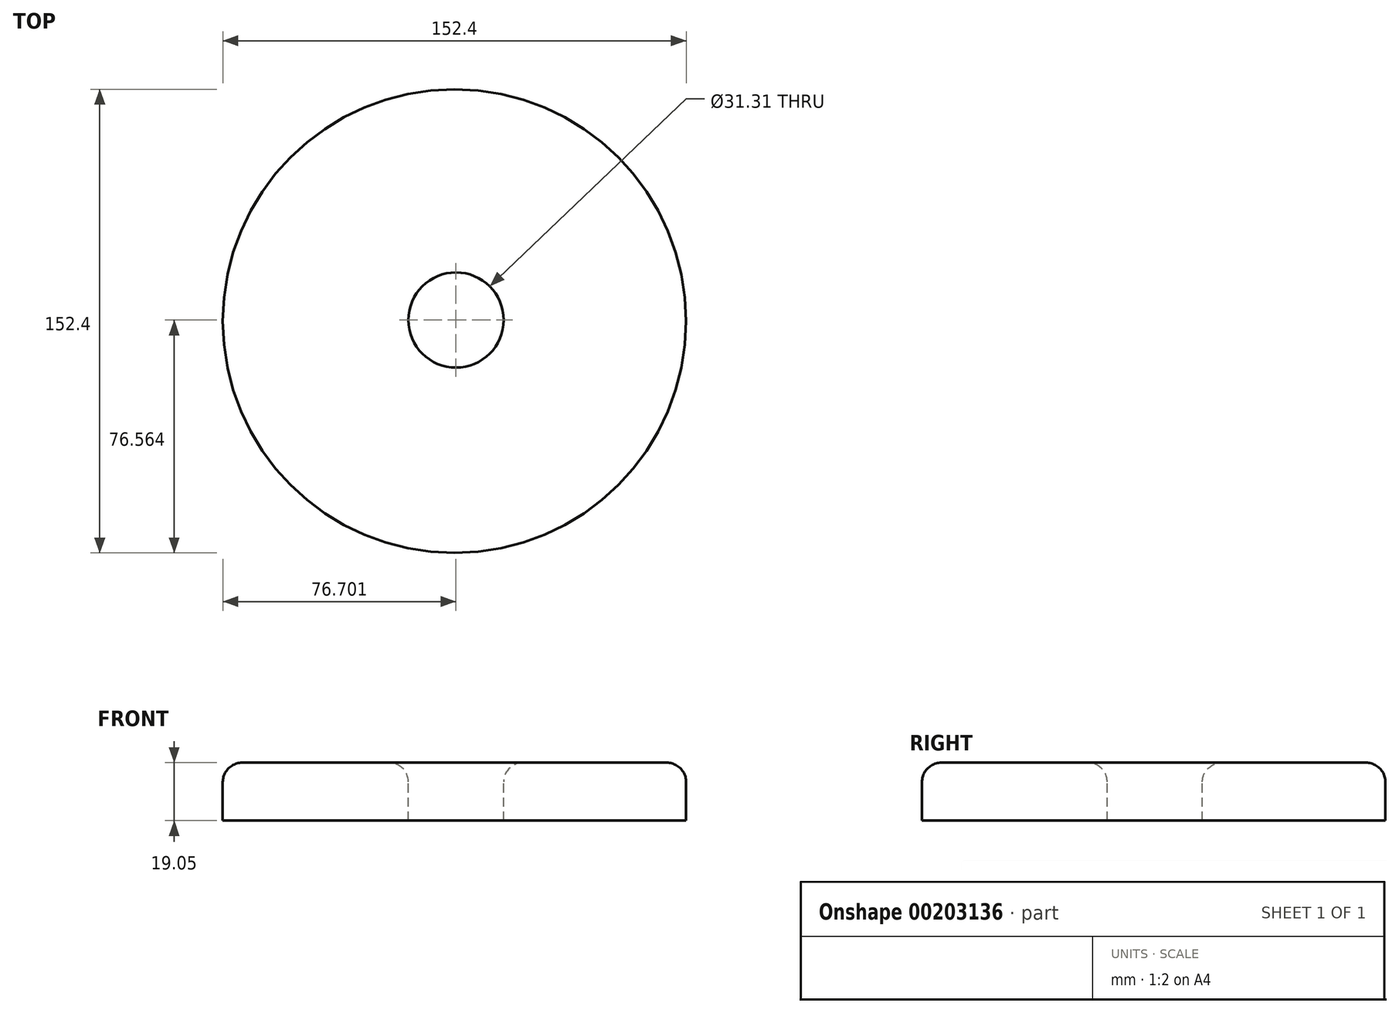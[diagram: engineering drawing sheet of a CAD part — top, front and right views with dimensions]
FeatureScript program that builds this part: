
annotation { "Feature Type Name" : "Feature", "Feature Type Description" : "" }
export const myFeature = defineFeature(function(context is Context, id is Id, definition is map)
    precondition{}
    {
        {
            var Q0;
            Q0=qCreatedBy(makeId("Top.planeOp"),FACE);
            var sketch = newSketch(context, id + "F0", { "sketchPlane" : qUnion([Q0])});
            skCircle(sketch, "E0", {"center": v(-0.28, 0.08) * mm, "radius": 76.2 * mm});
            skSolve(sketch);
        }
        {
            var Q0;
            Q0=makeQuery(id+"F0.imprint","IMPRINT",FACE,{"disambiguationData":[TD([[makeQuery(id+"F0.imprint","IMPRINT",EDGE,{"derivedFrom":sQuery(id+"F0.wireOp",EDGE,"E0")}),1.0]])]});
            extrude(context, id + "F1", {"entities" : qUnion([Q0]), "depth" : 19.05 * mm});
        }
        {
            var Q0;
            Q0=makeQuery(id+"F1.opExtrude","CAP_FACE",FACE,{"disambiguationData":[OSD([sQuery(id+"F0.wireOp",EDGE,"E0")])],"isStart":false});
            var sketch = newSketch(context, id + "F2", { "sketchPlane" : qUnion([Q0])});
            skCircle(sketch, "E1", {"center": v(0.22, 0.44) * mm, "radius": 15.65 * mm});
            skSolve(sketch);
        }
        {
            var Q0;
            Q0=makeQuery(id+"F2.imprint","IMPRINT",FACE,{"disambiguationData":[TD([[makeQuery(id+"F2.imprint","IMPRINT",EDGE,{"derivedFrom":sQuery(id+"F2.wireOp",EDGE,"E1")}),1.0]])]});
            var Q1;
            Q1=sQuery(id+"F2.wireOp",EDGE,"E1");
            extrude(context, id + "F3", {"entities" : qUnion([Q0]), "operationType" : NewBodyOperationType.REMOVE, "surfaceEntities" : qUnion([Q1]), "endBound" : BoundingType.THROUGH_ALL, "oppositeDirection" : true, "depth" : 25.4 * mm});
        }
        {
            var Q0;
            Q0=makeQuery(id+"F1.opExtrude","CAP_FACE",FACE,{"disambiguationData":[OSD([sQuery(id+"F0.wireOp",EDGE,"E0")])],"isStart":false});
            fillet(context, id + "F4", {"entities" : qUnion([Q0]), "radius" : 6.35 * mm, "tangentPropagation" : true, "allowEdgeOverflow" : false});
        }
    });
